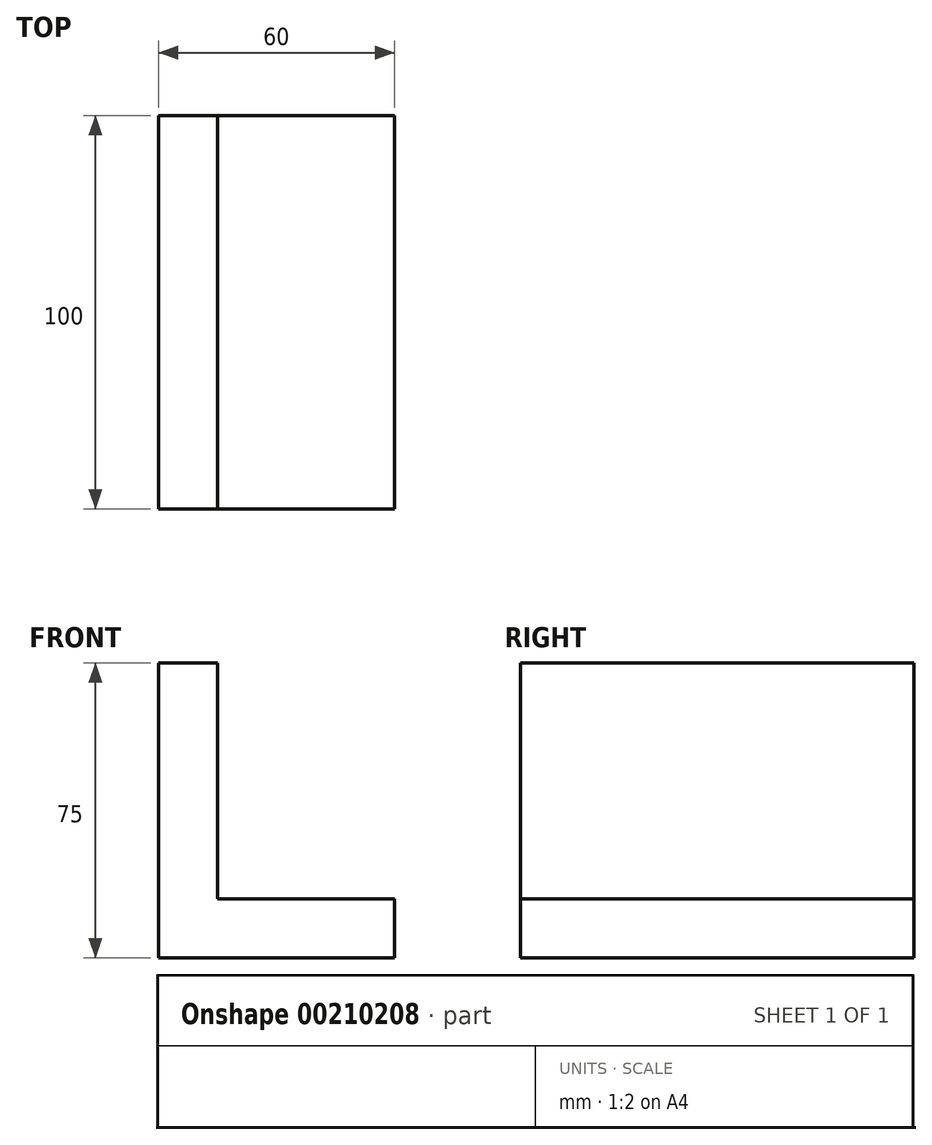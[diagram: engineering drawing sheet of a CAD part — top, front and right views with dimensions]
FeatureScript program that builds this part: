
annotation { "Feature Type Name" : "Feature", "Feature Type Description" : "" }
export const myFeature = defineFeature(function(context is Context, id is Id, definition is map)
    precondition{}
    {
        {
            var Q0;
            Q0=qCreatedBy(makeId("Front.planeOp"),FACE);
            var sketch = newSketch(context, id + "F0", { "sketchPlane" : qUnion([Q0])});
            skLineSegment(sketch, "E0", {"start": v(0, 0) * mm, "end": v(60, 0) * mm});
            skLineSegment(sketch, "E1", {"start": v(60, 0) * mm, "end": v(60, 15) * mm});
            skLineSegment(sketch, "E2", {"start": v(60, 15) * mm, "end": v(15, 15) * mm});
            skLineSegment(sketch, "E3", {"start": v(15, 15) * mm, "end": v(15, 75) * mm});
            skLineSegment(sketch, "E4", {"start": v(15, 75) * mm, "end": v(0, 75) * mm});
            skLineSegment(sketch, "E5", {"start": v(0, 75) * mm, "end": v(0, 0) * mm});
            skSolve(sketch);
        }
        {
            var Q0;
            Q0 = qSketchRegion(id + "F0", true);
            extrude(context, id + "F1", {"entities" : qUnion([Q0]), "depth" : 100 * mm});
        }
    });
